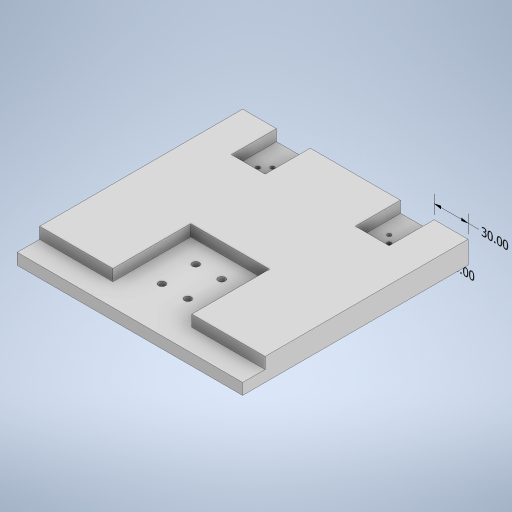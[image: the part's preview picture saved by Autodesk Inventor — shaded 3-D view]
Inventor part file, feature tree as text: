
AUTODESK INVENTOR PART (.ipt)
format: ipt  version: 2023 (Build 270158000, 158)  size: 315,392 bytes
history: native  units: mm
features: sketch x5, other x4, extrude x4, hole x1
ambient origin geometry x8: Origin, YZ Plane, XZ Plane, XY Plane, X Axis, Y Axis, Z Axis, Center Point
bodies: Body1 (feature_tree)
feature tree (14):
  other  "Sólido1"
  other  "Anotaciones"
  extrude  "Extrusión1"  Depth=200.0mm
  extrude  "Extrusión2"  Depth=10.0mm TaperAngle=0.0deg
  extrude  "Extrusión3"  Depth=20.0mm
  hole  "Agujero1"  [1 undecoded]
  extrude  "Extrusión4"  Depth=40.0mm
  sketch  "Boceto1"  dims[d0=200.0mm d1=200.0mm]
  sketch  "Boceto2"  dims[d2=20.0mm d3=0.0mm]
  sketch  "Boceto3"  dims[d4=20.0mm d5=20.0mm d6=30.0mm d7=30.0mm d8=20.0mm d9=35.0mm d10=35.0mm d11=69.0mm d12=10.0mm d13=0.0mm]
  sketch  "Boceto4"  dims[d14=20.0mm d15=0.0mm]
  sketch  "Boceto5"  dims[d16=3.5mm d18=1.75mm d19=1.75mm d20=1.75mm d21=1.75mm d22=10.0mm d23=10.0mm d25=20.0mm d26=40.0mm d27=40.0mm d28=3.5mm d29=6.0mm d30=4.0mm d31=2.0mm d32=90.0deg d33=8.0mm d34=20.594885mm d38=10.0mm d39=10.0mm d40=40.0mm d41=10.0mm d42=0.0mm d43=6.672192mm d44=4.931866mm d45=30.0mm d46=5.890777mm d47=4.508932mm d48=30.0mm]
  other  "Cota lineal 1"
  other  "Cota lineal 2"
note: 1 required parameter value undecoded (feature->parameter linkage not recoverable at this tier; creation-order binding heuristic only, values carry confidence <= 0.55)
